# Revit family: Qf_Vollrath_HDC9336_Heated_Display_Case_Cubed_Countertop-36 inches_cat
name_source: partatom
category: Specialty Equipment
units: mm (PartAtom-declared; Revit-internal decimal feet)

## family parameters
Always vertical = Yes
Cut with Voids When Loaded = No
Part Type = Normal
Room Calculation Point = No
Round Connector Dimension = Use Diameter
Shared = No
Work Plane-Based = No

## types (1)
- Qf_Vollrath_HDC9336_Heated_Display_Case_Cubed_Countertop-36 inches_cat
    Apparent Power = 0 VA
    Conn Conduit = Yes
    Conn Plug = NEMA 5-15P
    Cycle = 50 Hz
    Depth = 21.5 "
    Description = Heated Display Case Cubed Countertop-36"
    Elec Conn Connection Height = 0 "
    Elec Conn RI Height = 0 "
    FL Amps = 6 A
    Foodservice Equipment Identifier = Yes
    Height = 37 "
    Identify Quantity as Lot = Yes
    Length = 35.9 "
    Manufacturer = Vollrath
    Max Overcurrent Protection = 0 A
    Min Ckt Ampacity = 0 A
    Model = HDC9336
    Number of Poles = 1
    Phase = 0
    Volts = 120 V
    Watts = 696 W
    Weight in Pounds = 347

## geometry (parser evidence)
native form markers: Sweep x2
no freeform markers — native parametric forms only
